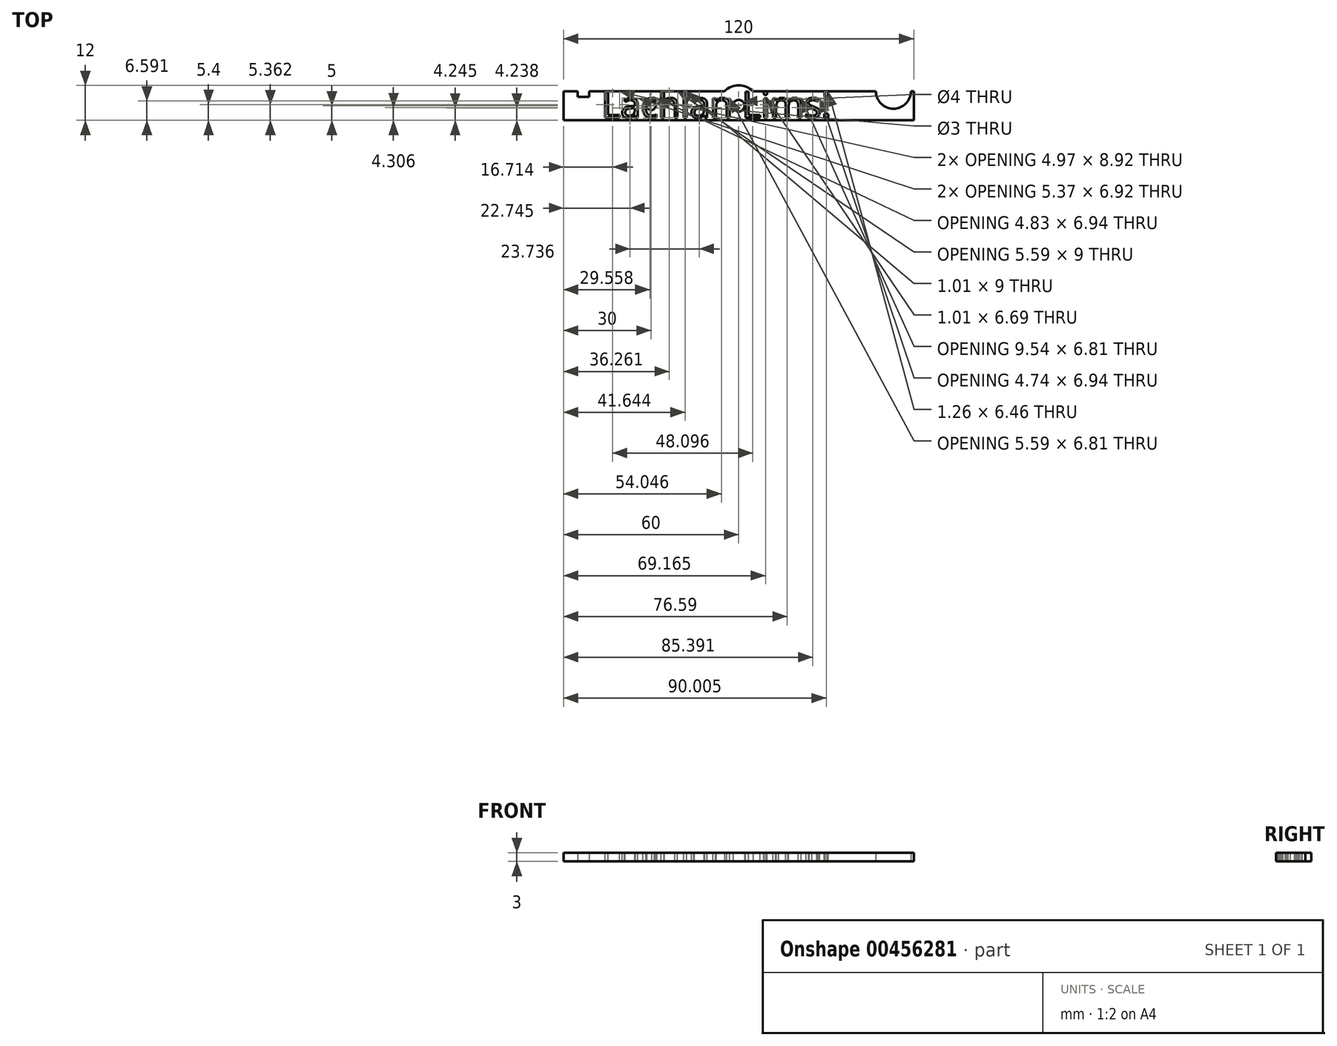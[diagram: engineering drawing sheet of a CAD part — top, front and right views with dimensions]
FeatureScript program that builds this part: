
annotation { "Feature Type Name" : "Feature", "Feature Type Description" : "" }
export const myFeature = defineFeature(function(context is Context, id is Id, definition is map)
    precondition{}
    {
        {
            var Q0;
            Q0=qCreatedBy(makeId("Top.planeOp"),FACE);
            var sketch = newSketch(context, id + "F0", { "sketchPlane" : qUnion([Q0])});
            skLineSegment(sketch, "E0.bottom", {"start": v(-60, 5) * mm, "end": v(60, 5) * mm});
            skLineSegment(sketch, "E0.top", {"start": v(-60, -5) * mm, "end": v(60, -5) * mm});
            skLineSegment(sketch, "E0.left", {"start": v(-60, 5) * mm, "end": v(-60, -5) * mm});
            skLineSegment(sketch, "E0.right", {"start": v(60, 5) * mm, "end": v(60, -5) * mm});
            skPoint(sketch, "E0.middle", {"position": v(0, 0) * mm});
            skLineSegment(sketch, "E1.bottom", {"start": v(-51.23, 5) * mm, "end": v(-55.23, 5) * mm});
            skLineSegment(sketch, "E1.top", {"start": v(-51.23, 3) * mm, "end": v(-55.23, 3) * mm});
            skLineSegment(sketch, "E1.left", {"start": v(-51.23, 5) * mm, "end": v(-51.23, 3) * mm});
            skLineSegment(sketch, "E1.right", {"start": v(-55.23, 5) * mm, "end": v(-55.23, 3) * mm});
            skCircle(sketch, "E2", {"center": v(0, 0) * mm, "radius": 7 * mm});
            skCircle(sketch, "E3", {"center": v(-30, 0) * mm, "radius": 1.5 * mm});
            skCircle(sketch, "E4", {"center": v(0, 0) * mm, "radius": 2 * mm});
            skCircle(sketch, "E5", {"center": v(53, 5) * mm, "radius": 6 * mm});
            skSolve(sketch);
        }
        {
            var Q0;
            {var subQ0=sQuery(id+"F0.wireOp",EDGE,"E0.right");Q0=makeQuery(id+"F0.imprint","IMPRINT",FACE,{"disambiguationData":[TD([[makeQuery(id+"F0.imprint","IMPRINT",EDGE,{"derivedFrom":subQ0}),-1.0]])]});}
            var Q1;
            Q1=makeQuery(id+"F0.imprint","IMPRINT",FACE,{"disambiguationData":[TD([[makeQuery(id+"F0.imprint","IMPRINT",EDGE,{"derivedFrom":sQuery(id+"F0.wireOp",EDGE,"E4")}),-1.0]])]});
            var Q2;
            {var subQ0=sQuery(id+"F0.wireOp",EDGE,"E2");var subQ1=sQuery(id+"F0.wireOp",EDGE,"E0.bottom");var subQ2=makeQuery(id+"F0.imprint","INTERSECT",VERTEX,{"disambiguationData":[OD(0.0)],"derivedFrom":[subQ1,subQ0]});Q2=makeQuery(id+"F0.imprint","IMPRINT",FACE,{"disambiguationData":[TD([[makeQuery(id+"F0.imprint","IMPRINT",EDGE,{"disambiguationData":[TD([[subQ2,-1.0]])],"derivedFrom":subQ1}),1.0]])]});}
            var Q3;
            {var subQ0=sQuery(id+"F0.wireOp",EDGE,"E2");var subQ1=sQuery(id+"F0.wireOp",EDGE,"E0.top");var subQ2=makeQuery(id+"F0.imprint","INTERSECT",VERTEX,{"disambiguationData":[OD(0.0)],"derivedFrom":[subQ1,subQ0]});Q3=makeQuery(id+"F0.imprint","IMPRINT",FACE,{"disambiguationData":[TD([[makeQuery(id+"F0.imprint","IMPRINT",EDGE,{"disambiguationData":[TD([[subQ2,-1.0]])],"derivedFrom":subQ1}),-1.0]])]});}
            var Q4;
            {var subQ0=sQuery(id+"F0.wireOp",EDGE,"E0.left");Q4=makeQuery(id+"F0.imprint","IMPRINT",FACE,{"disambiguationData":[TD([[makeQuery(id+"F0.imprint","IMPRINT",EDGE,{"derivedFrom":subQ0}),1.0]])]});}
            extrude(context, id + "F1", {"entities" : qUnion([Q0, Q1, Q2, Q3, Q4]), "depth" : 3 * mm});
        }
        {
            var Q0;
            Q0=makeQuery(id+"F1.opExtrude","CAP_FACE",FACE,{"disambiguationData":[OSD([sQuery(id+"F0.wireOp",EDGE,"E0.bottom"),sQuery(id+"F0.wireOp",EDGE,"E0.top"),sQuery(id+"F0.wireOp",EDGE,"E0.left"),sQuery(id+"F0.wireOp",EDGE,"E0.right"),sQuery(id+"F0.wireOp",EDGE,"E1.top"),sQuery(id+"F0.wireOp",EDGE,"E1.left"),sQuery(id+"F0.wireOp",EDGE,"E1.right"),sQuery(id+"F0.wireOp",EDGE,"E2"),sQuery(id+"F0.wireOp",EDGE,"E3"),sQuery(id+"F0.wireOp",EDGE,"E4"),sQuery(id+"F0.wireOp",EDGE,"E5")])],"isStart":false});
            var sketch = newSketch(context, id + "F2", { "sketchPlane" : qUnion([Q0])});
            skText(sketch, "E6", { "text": "Lachlan Lims!\n", "fontName": "OpenSans-Regular.ttf"});
            skLineSegment(sketch, "E7", {"start": v(-60, 0.4) * mm, "end": v(-47, 0.4) * mm, "construction": true});
            skLineSegment(sketch, "E8", {"start": v(-26.54, 4.9) * mm, "end": v(-25.52, 4.9) * mm});
            skLineSegment(sketch, "E9", {"start": v(-18.99, 4.9) * mm, "end": v(-17.75, 4.9) * mm});
            skCircle(sketch, "E10", {"center": v(9.17, 4.29) * mm, "radius": 0.63 * mm});
            const initialGuessF2  = {"E6": [-0.047, -0.0041, 1, 0, 0.009]};
            skSetInitialGuess(sketch, initialGuessF2);
            skSolve(sketch);
        }
        {
            var Q0;
            {var subQ0=sQuery(id+"F2.wireOp",EDGE,"E6.sketch_text.stroke-128");Q0=makeQuery(id+"F2.imprint","IMPRINT",FACE,{"disambiguationData":[TD([[makeQuery(id+"F2.imprint","IMPRINT",EDGE,{"derivedFrom":subQ0}),-1.0]])]});}
            var Q1;
            Q1=makeQuery(id+"F2.imprint","IMPRINT",FACE,{"disambiguationData":[TD([[makeQuery(id+"F2.imprint","IMPRINT",EDGE,{"derivedFrom":sQuery(id+"F2.wireOp",EDGE,"E6.sketch_text.stroke-120")}),-1.0]])]});
            var Q2;
            Q2=makeQuery(id+"F2.imprint","IMPRINT",FACE,{"disambiguationData":[TD([[makeQuery(id+"F2.imprint","IMPRINT",EDGE,{"derivedFrom":sQuery(id+"F2.wireOp",EDGE,"E6.sketch_text.stroke-132")}),-1.0]])]});
            var Q3;
            Q3=makeQuery(id+"F2.imprint","IMPRINT",FACE,{"disambiguationData":[TD([[makeQuery(id+"F2.imprint","IMPRINT",EDGE,{"derivedFrom":sQuery(id+"F2.wireOp",EDGE,"E6.sketch_text.stroke-160")}),-1.0]])]});
            var Q4;
            Q4=makeQuery(id+"F2.imprint","IMPRINT",FACE,{"disambiguationData":[TD([[makeQuery(id+"F2.imprint","IMPRINT",EDGE,{"derivedFrom":sQuery(id+"F2.wireOp",EDGE,"E6.sketch_text.stroke-185")}),-1.0]])]});
            var Q5;
            Q5=makeQuery(id+"F2.imprint","IMPRINT",FACE,{"disambiguationData":[TD([[makeQuery(id+"F2.imprint","IMPRINT",EDGE,{"derivedFrom":sQuery(id+"F2.wireOp",EDGE,"E6.sketch_text.stroke-189")}),-1.0]])]});
            var Q6;
            Q6=makeQuery(id+"F2.imprint","IMPRINT",FACE,{"disambiguationData":[TD([[makeQuery(id+"F2.imprint","IMPRINT",EDGE,{"derivedFrom":sQuery(id+"F2.wireOp",EDGE,"E6.sketch_text.stroke-114")}),-1.0]])]});
            var Q7;
            Q7=makeQuery(id+"F2.imprint","IMPRINT",FACE,{"disambiguationData":[TD([[makeQuery(id+"F2.imprint","IMPRINT",EDGE,{"derivedFrom":sQuery(id+"F2.wireOp",EDGE,"E6.sketch_text.stroke-97")}),-1.0]])]});
            var Q8;
            Q8=makeQuery(id+"F2.imprint","IMPRINT",FACE,{"disambiguationData":[TD([[makeQuery(id+"F2.imprint","IMPRINT",EDGE,{"derivedFrom":sQuery(id+"F2.wireOp",EDGE,"E6.sketch_text.stroke-70")}),-1.0]])]});
            var Q9;
            {var subQ0=sQuery(id+"F2.wireOp",EDGE,"E6.sketch_text.stroke-66");Q9=makeQuery(id+"F2.imprint","IMPRINT",FACE,{"disambiguationData":[TD([[makeQuery(id+"F2.imprint","IMPRINT",EDGE,{"derivedFrom":subQ0}),-1.0]])]});}
            var Q10;
            Q10=makeQuery(id+"F2.imprint","IMPRINT",FACE,{"disambiguationData":[TD([[makeQuery(id+"F2.imprint","IMPRINT",EDGE,{"derivedFrom":sQuery(id+"F2.wireOp",EDGE,"E6.sketch_text.stroke-48")}),-1.0]])]});
            var Q11;
            Q11=makeQuery(id+"F2.imprint","IMPRINT",FACE,{"disambiguationData":[TD([[makeQuery(id+"F2.imprint","IMPRINT",EDGE,{"derivedFrom":sQuery(id+"F2.wireOp",EDGE,"E6.sketch_text.stroke-33")}),-1.0]])]});
            var Q12;
            Q12=makeQuery(id+"F2.imprint","IMPRINT",FACE,{"disambiguationData":[TD([[makeQuery(id+"F2.imprint","IMPRINT",EDGE,{"derivedFrom":sQuery(id+"F2.wireOp",EDGE,"E6.sketch_text.stroke-6")}),-1.0]])]});
            var Q13;
            Q13=makeQuery(id+"F2.imprint","IMPRINT",FACE,{"disambiguationData":[TD([[makeQuery(id+"F2.imprint","IMPRINT",EDGE,{"derivedFrom":sQuery(id+"F2.wireOp",EDGE,"E6.sketch_text.stroke-0")}),-1.0]])]});
            extrude(context, id + "F3", {"entities" : qUnion([Q0, Q1, Q2, Q3, Q4, Q5, Q6, Q7, Q8, Q9, Q10, Q11, Q12, Q13]), "operationType" : NewBodyOperationType.REMOVE, "oppositeDirection" : true, "depth" : 25 * mm});
        }
        {
            var Q0;
            Q0=makeQuery(id+"F3.boolean.opBoolean","COPY",EDGE,{"derivedFrom":makeQuery(id+"F3.opExtrude","SWEPT_EDGE",EDGE,{"disambiguationData":[OSD([sQuery(id+"F2.wireOp",EDGE,"E6.sketch_text.stroke-124"),sQuery(id+"F2.wireOp",EDGE,"E10")])]})});
            var Q1;
            Q1=makeQuery(id+"F3.boolean.opBoolean","COPY",EDGE,{"derivedFrom":makeQuery(id+"F3.opExtrude","SWEPT_EDGE",EDGE,{"disambiguationData":[OSD([sQuery(id+"F2.wireOp",EDGE,"E6.sketch_text.stroke-124"),sQuery(id+"F2.wireOp",EDGE,"E6.sketch_text.stroke-131")])]})});
            var Q2;
            Q2=makeQuery(id+"F3.boolean.opBoolean","COPY",EDGE,{"derivedFrom":makeQuery(id+"F3.opExtrude","SWEPT_EDGE",EDGE,{"disambiguationData":[OSD([sQuery(id+"F2.wireOp",EDGE,"E6.sketch_text.stroke-127"),sQuery(id+"F2.wireOp",EDGE,"E10")])]})});
            var Q3;
            Q3=makeQuery(id+"F3.boolean.opBoolean","COPY",EDGE,{"derivedFrom":makeQuery(id+"F3.opExtrude","SWEPT_EDGE",EDGE,{"disambiguationData":[OSD([sQuery(id+"F2.wireOp",EDGE,"E6.sketch_text.stroke-127"),sQuery(id+"F2.wireOp",EDGE,"E6.sketch_text.stroke-128")])]})});
            fillet(context, id + "F4", {"entities" : qUnion([Q0, Q1, Q2, Q3]), "radius" : .5 * mm, "tangentPropagation" : true, "allowEdgeOverflow" : false});
        }
    });
